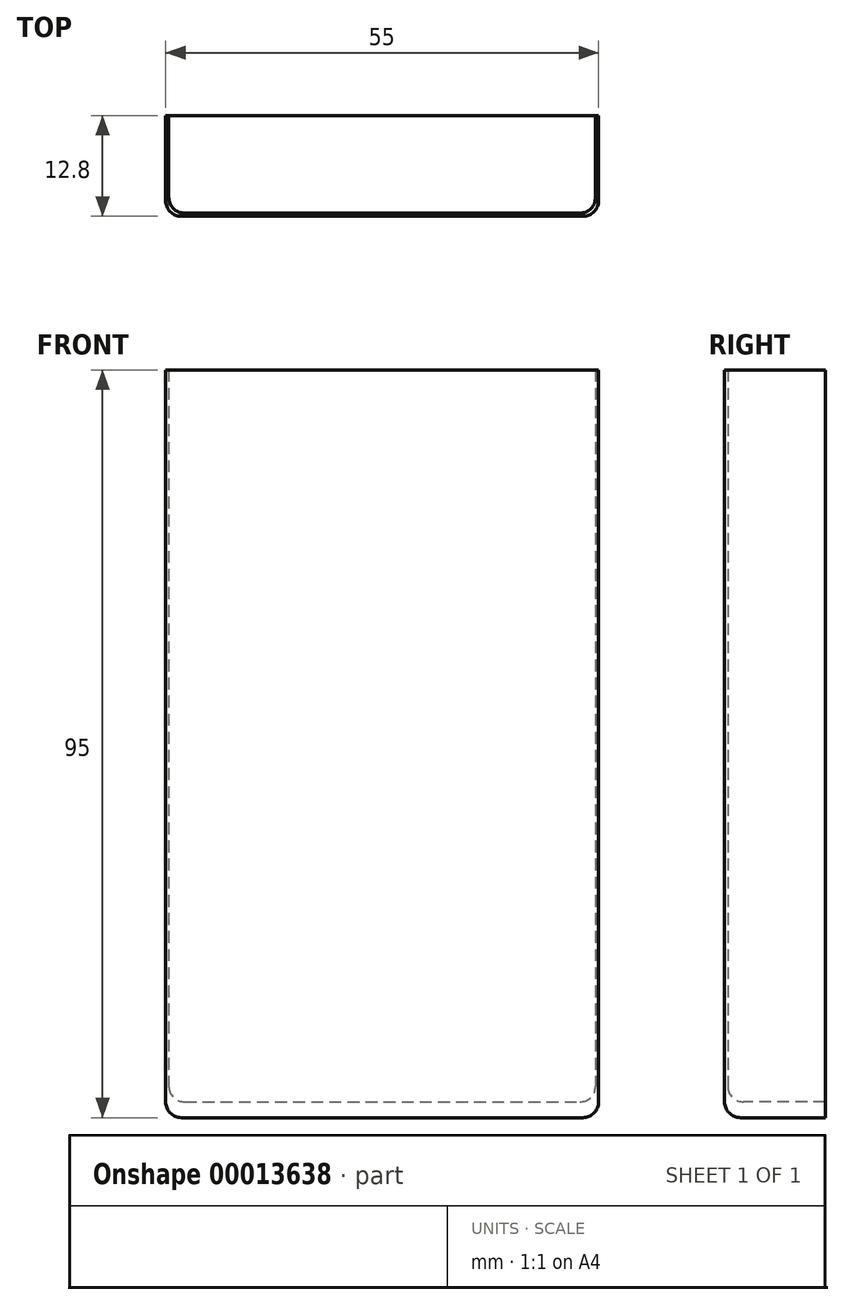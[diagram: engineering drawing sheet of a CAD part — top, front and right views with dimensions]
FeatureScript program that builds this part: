
annotation { "Feature Type Name" : "Feature", "Feature Type Description" : "" }
export const myFeature = defineFeature(function(context is Context, id is Id, definition is map)
    precondition{}
    {
        {
            var Q0;
            Q0=qCreatedBy(makeId("Top.planeOp"),FACE);
            var sketch = newSketch(context, id + "F0", { "sketchPlane" : qUnion([Q0])});
            skLineSegment(sketch, "E0.bottom", {"start": v(-27.5, 6.4) * mm, "end": v(27.5, 6.4) * mm});
            skLineSegment(sketch, "E0.top", {"start": v(-27.5, -6.4) * mm, "end": v(27.5, -6.4) * mm});
            skLineSegment(sketch, "E0.left", {"start": v(-27.5, 6.4) * mm, "end": v(-27.5, -6.4) * mm});
            skLineSegment(sketch, "E0.right", {"start": v(27.5, 6.4) * mm, "end": v(27.5, -6.4) * mm});
            skPoint(sketch, "E1", {"position": v(-27.5, 0) * mm});
            skPoint(sketch, "E2", {"position": v(0, 6.4) * mm});
            skSolve(sketch);
        }
        {
            var Q0;
            Q0=makeQuery(id+"F0.imprint","IMPRINT",FACE,{"disambiguationData":[TD([[makeQuery(id+"F0.imprint","IMPRINT",EDGE,{"derivedFrom":sQuery(id+"F0.wireOp",EDGE,"E0.bottom")}),-1.0]])]});
            extrude(context, id + "F1", {"entities" : qUnion([Q0]), "depth" : 95 * mm});
        }
        {
            var Q0;
            Q0=makeQuery(id+"F1.opExtrude","CAP_FACE",FACE,{"disambiguationData":[OSD([sQuery(id+"F0.wireOp",EDGE,"E0.bottom"),sQuery(id+"F0.wireOp",EDGE,"E0.top"),sQuery(id+"F0.wireOp",EDGE,"E0.left"),sQuery(id+"F0.wireOp",EDGE,"E0.right")])],"isStart":false});
            var Q1;
            Q1=makeQuery(id+"F1.opExtrude","SWEPT_FACE",FACE,{"disambiguationData":[OSD([sQuery(id+"F0.wireOp",EDGE,"E0.bottom")])]});
            shell(context, id + "F2", {"entities" : qUnion([Q0, Q1]), "thickness" : .4 * mm});
        }
        {
            var Q0;
            Q0=makeQuery(id+"F1.opExtrude","CAP_FACE",FACE,{"disambiguationData":[OSD([sQuery(id+"F0.wireOp",EDGE,"E0.bottom"),sQuery(id+"F0.wireOp",EDGE,"E0.top"),sQuery(id+"F0.wireOp",EDGE,"E0.left"),sQuery(id+"F0.wireOp",EDGE,"E0.right")])],"isStart":true});
            extrude(context, id + "F3", {"entities" : qUnion([Q0]), "operationType" : NewBodyOperationType.ADD, "oppositeDirection" : true, "depth" : 2 * mm});
        }
        {
            var Q0;
            Q0=makeQuery(id+"F2.opShell","OFFSET_EDGE",EDGE,{"disambiguationData":[OSD([sQuery(id+"F0.wireOp",EDGE,"E0.top"),sQuery(id+"F0.wireOp",EDGE,"E0.left")])]});
            var Q1;
            Q1=makeQuery(id+"F2.opShell","OFFSET_EDGE",EDGE,{"disambiguationData":[OSD([sQuery(id+"F0.wireOp",EDGE,"E0.top"),sQuery(id+"F0.wireOp",EDGE,"E0.right")])]});
            var Q2;
            Q2=makeQuery(id+"F1.opExtrude","SWEPT_EDGE",EDGE,{"disambiguationData":[OSD([sQuery(id+"F0.wireOp",EDGE,"E0.top"),sQuery(id+"F0.wireOp",EDGE,"E0.left")])]});
            var Q3;
            Q3=makeQuery(id+"F1.opExtrude","SWEPT_EDGE",EDGE,{"disambiguationData":[OSD([sQuery(id+"F0.wireOp",EDGE,"E0.top"),sQuery(id+"F0.wireOp",EDGE,"E0.right")])]});
            var Q4;
            Q4=makeQuery(id+"F1.opExtrude","CAP_EDGE",EDGE,{"disambiguationData":[OSD([sQuery(id+"F0.wireOp",EDGE,"E0.top")])],"isStart":true});
            var Q5;
            Q5=makeQuery(id+"F1.opExtrude","CAP_EDGE",EDGE,{"disambiguationData":[OSD([sQuery(id+"F0.wireOp",EDGE,"E0.left")])],"isStart":true});
            var Q6;
            Q6=makeQuery(id+"F1.opExtrude","CAP_EDGE",EDGE,{"disambiguationData":[OSD([sQuery(id+"F0.wireOp",EDGE,"E0.right")])],"isStart":true});
            var Q7;
            {var subQ0=sQuery(id+"F0.wireOp",EDGE,"E0.top");Q7=makeQuery(id+"F3.boolean.opBoolean","INTERSECT",EDGE,{"derivedFrom":[makeQuery(id+"F2.opShell","OFFSET_FACE",FACE,{"disambiguationData":[OSD([subQ0])]}),makeQuery(id+"F3.opExtrude","CAP_FACE",FACE,{"disambiguationData":[OSD([sQuery(id+"F0.wireOp",EDGE,"E0.bottom"),subQ0,sQuery(id+"F0.wireOp",EDGE,"E0.left"),sQuery(id+"F0.wireOp",EDGE,"E0.right")])],"isStart":false})]});}
            var Q8;
            {var subQ0=sQuery(id+"F0.wireOp",EDGE,"E0.right");Q8=makeQuery(id+"F3.boolean.opBoolean","INTERSECT",EDGE,{"derivedFrom":[makeQuery(id+"F2.opShell","OFFSET_FACE",FACE,{"disambiguationData":[OSD([subQ0])]}),makeQuery(id+"F3.opExtrude","CAP_FACE",FACE,{"disambiguationData":[OSD([sQuery(id+"F0.wireOp",EDGE,"E0.bottom"),sQuery(id+"F0.wireOp",EDGE,"E0.top"),sQuery(id+"F0.wireOp",EDGE,"E0.left"),subQ0])],"isStart":false})]});}
            var Q9;
            {var subQ0=sQuery(id+"F0.wireOp",EDGE,"E0.left");Q9=makeQuery(id+"F3.boolean.opBoolean","INTERSECT",EDGE,{"derivedFrom":[makeQuery(id+"F2.opShell","OFFSET_FACE",FACE,{"disambiguationData":[OSD([subQ0])]}),makeQuery(id+"F3.opExtrude","CAP_FACE",FACE,{"disambiguationData":[OSD([sQuery(id+"F0.wireOp",EDGE,"E0.bottom"),sQuery(id+"F0.wireOp",EDGE,"E0.top"),subQ0,sQuery(id+"F0.wireOp",EDGE,"E0.right")])],"isStart":false})]});}
            fillet(context, id + "F4", {"entities" : qUnion([Q0, Q1, Q2, Q3, Q4, Q5, Q6, Q7, Q8, Q9]), "radius" : 2 * mm, "allowEdgeOverflow" : false});
        }
    });
